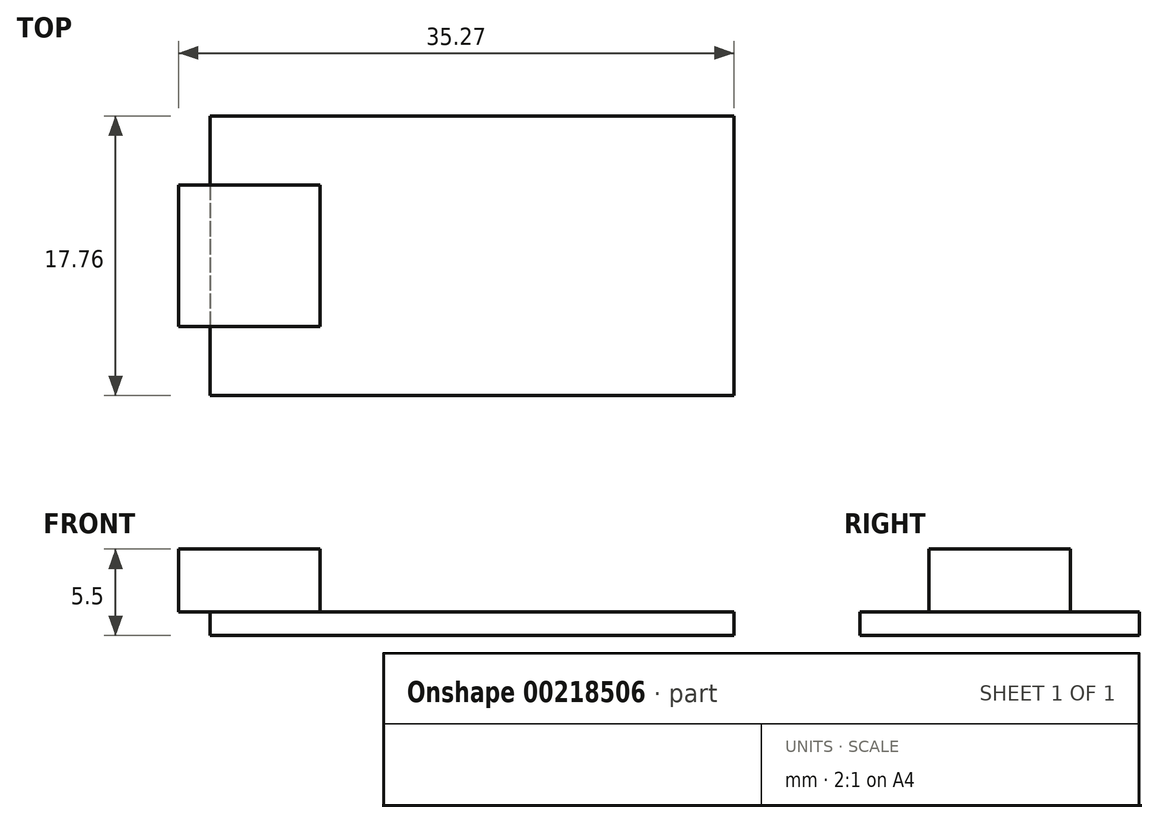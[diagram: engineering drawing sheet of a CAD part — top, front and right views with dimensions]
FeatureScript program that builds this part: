
annotation { "Feature Type Name" : "Feature", "Feature Type Description" : "" }
export const myFeature = defineFeature(function(context is Context, id is Id, definition is map)
    precondition{}
    {
        {
            var Q0;
            Q0=qCreatedBy(makeId("Top.planeOp"),FACE);
            var sketch = newSketch(context, id + "F0", { "sketchPlane" : qUnion([Q0])});
            skLineSegment(sketch, "E0.bottom", {"start": v(-16.63, 8.88) * mm, "end": v(16.63, 8.88) * mm});
            skLineSegment(sketch, "E0.top", {"start": v(-16.63, -8.88) * mm, "end": v(16.63, -8.88) * mm});
            skLineSegment(sketch, "E0.left", {"start": v(-16.63, 8.88) * mm, "end": v(-16.63, -8.88) * mm});
            skLineSegment(sketch, "E0.right", {"start": v(16.63, 8.88) * mm, "end": v(16.63, -8.88) * mm});
            skPoint(sketch, "E1", {"position": v(0, 8.88) * mm});
            skPoint(sketch, "E2", {"position": v(-16.63, 0) * mm});
            skSolve(sketch);
        }
        {
            var Q0;
            Q0 = qSketchRegion(id + "F0", true);
            extrude(context, id + "F1", {"entities" : qUnion([Q0]), "depth" : 1.5 * mm});
        }
        {
            var Q0;
            Q0=makeQuery(id+"F1.opExtrude","SWEPT_FACE",FACE,{"disambiguationData":[OSD([sQuery(id+"F0.wireOp",EDGE,"E0.left")])]});
            var sketch = newSketch(context, id + "F2", { "sketchPlane" : qUnion([Q0])});
            skLineSegment(sketch, "E3.bottom", {"start": v(-4.5, 1.5) * mm, "end": v(4.5, 1.5) * mm});
            skLineSegment(sketch, "E3.top", {"start": v(-4.5, 5.5) * mm, "end": v(4.5, 5.5) * mm});
            skLineSegment(sketch, "E3.left", {"start": v(-4.5, 1.5) * mm, "end": v(-4.5, 5.5) * mm});
            skLineSegment(sketch, "E3.right", {"start": v(4.5, 1.5) * mm, "end": v(4.5, 5.5) * mm});
            skPoint(sketch, "E4", {"position": v(0, 5.5) * mm});
            skSolve(sketch);
        }
        {
            var Q0;
            Q0=makeQuery(id+"F2.imprint","IMPRINT",FACE,{"disambiguationData":[TD([[makeQuery(id+"F2.imprint","IMPRINT",EDGE,{"derivedFrom":sQuery(id+"F2.wireOp",EDGE,"E3.bottom")}),1.0]])]});
            extrude(context, id + "F3", {"entities" : qUnion([Q0]), "depth" : 2 * mm});
        }
        {
            var Q0;
            Q0=makeQuery(id+"F3.opExtrude","CAP_FACE",FACE,{"disambiguationData":[OSD([sQuery(id+"F2.wireOp",EDGE,"E3.bottom"),sQuery(id+"F2.wireOp",EDGE,"E3.top"),sQuery(id+"F2.wireOp",EDGE,"E3.left"),sQuery(id+"F2.wireOp",EDGE,"E3.right")])],"isStart":true});
            extrude(context, id + "F4", {"entities" : qUnion([Q0]), "operationType" : NewBodyOperationType.ADD, "depth" : 7 * mm});
        }
    });
